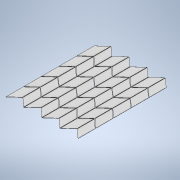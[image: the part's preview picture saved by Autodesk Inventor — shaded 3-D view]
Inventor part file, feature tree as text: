
AUTODESK INVENTOR PART (.ipt)
format: ipt  version: 2020 (Build 240168000, 168)  size: 354,304 bytes
history: native  units: mm
features: extrude x1, sketch x1
ambient origin geometry x8: Origin, YZ Plane, XZ Plane, XY Plane, X Axis, Y Axis, Z Axis, Center Point
bodies: Solid1 (feature_tree)
feature tree (2):
  extrude  "Extrusion1"  Depth=0.6mm
  sketch  "Sketch1"  dims[d0=47.0mm d1=22.0mm d2=24.0mm d3=47.0mm d4=0.675mm d5=47.0mm d6=22.0mm d7=24.0mm d8=47.0mm d9=0.675mm d10=47.0mm d11=22.0mm d12=24.0mm d13=47.0mm d14=0.675mm d15=47.0mm d16=47.0mm d17=22.0mm d18=24.0mm d19=47.0mm d20=0.675mm d21=47.0mm d22=22.0mm d23=24.0mm d24=47.0mm d25=0.675mm d26=47.0mm d27=22.0mm d28=24.0mm d29=47.0mm d30=0.675mm d31=47.0mm d32=47.0mm d33=22.0mm d34=24.0mm d35=47.0mm d36=0.675mm d37=47.0mm d38=22.0mm d39=24.0mm d40=47.0mm d41=0.675mm d42=47.0mm d43=22.0mm d44=24.0mm d45=47.0mm d46=0.675mm d47=47.0mm d48=47.0mm d49=22.0mm d50=24.0mm d51=47.0mm d52=0.675mm d53=47.0mm d54=22.0mm d55=24.0mm d56=47.0mm d57=0.675mm d58=47.0mm d59=22.0mm d60=24.0mm d61=47.0mm d62=0.675mm d63=47.0mm d71=47.0mm d72=47.0mm d73=47.0mm d74=47.0mm d75=47.0mm d76=0.6mm d77=0.0mm]
